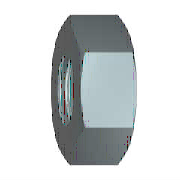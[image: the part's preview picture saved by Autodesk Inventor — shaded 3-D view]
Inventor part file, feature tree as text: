
AUTODESK INVENTOR PART (.ipt)
format: ipt  version: 2020 (Build 240168000, 168)  size: 163,840 bytes
history: native  units: mm (DEFAULTED — no unit token found)
features: sketch x3, other x2, extrude x1, hole x1, plane x1
ambient origin geometry x7: Origin, YZ Plane, XZ Plane, X Axis, Y Axis, Z Axis, Center Point
bodies: Solid1 (feature_tree)
feature tree (8):
  extrude  "Bryła"  Depth=9.237604mm
  other  "Faza1"
  hole  "Gwint"  [1 undecoded]
  other  "Work Axis1"
  plane  "Work Plane1"
  sketch  "Szkic1"
  sketch  "Szkic2"
  sketch  "Szkic3"
note: 1 required parameter value undecoded (feature->parameter linkage not recoverable at this tier; creation-order binding heuristic only, values carry confidence <= 0.55)
